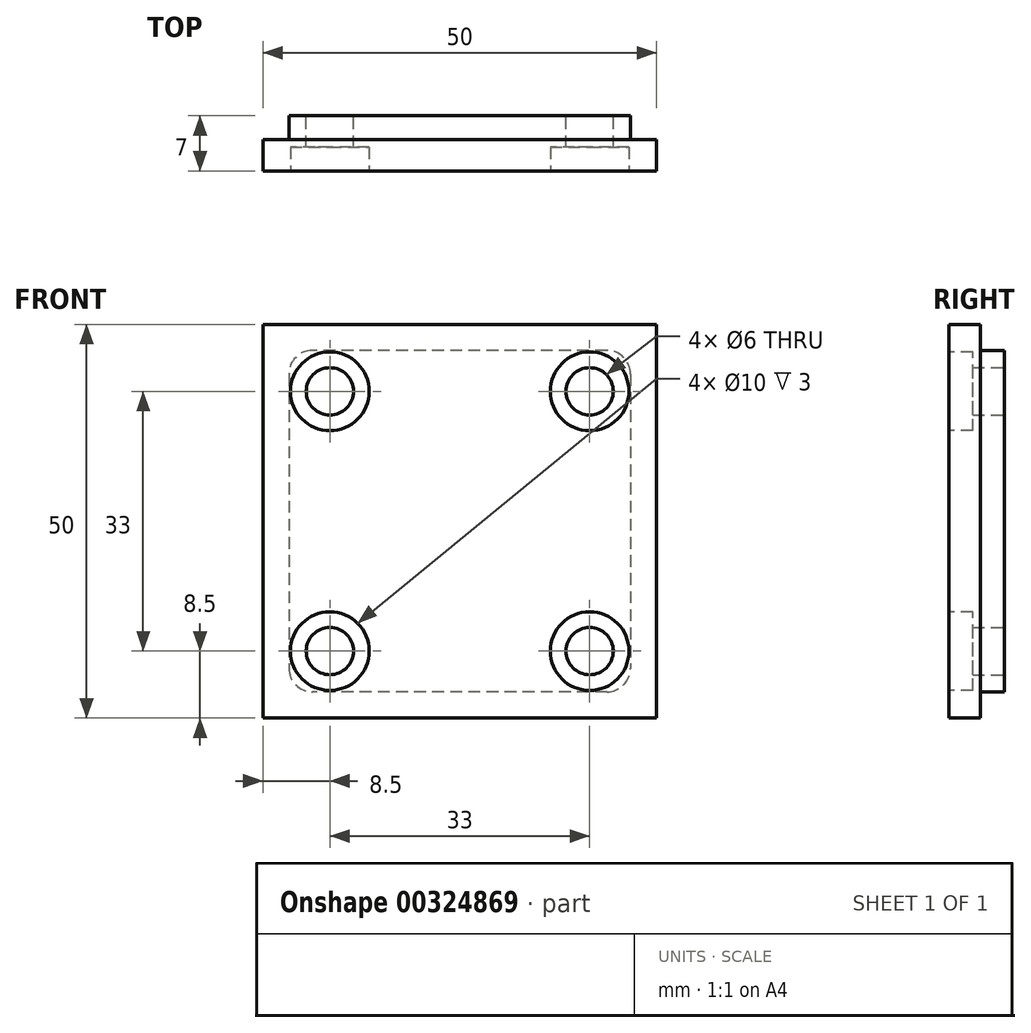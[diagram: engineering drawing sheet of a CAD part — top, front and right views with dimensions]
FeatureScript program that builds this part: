
annotation { "Feature Type Name" : "Feature", "Feature Type Description" : "" }
export const myFeature = defineFeature(function(context is Context, id is Id, definition is map)
    precondition{}
    {
        {
            var Q0;
            Q0=qCreatedBy(makeId("Front.planeOp"),FACE);
            var sketch = newSketch(context, id + "F0", { "sketchPlane" : qUnion([Q0])});
            skLineSegment(sketch, "E0.bottom", {"start": v(-25, 25) * mm, "end": v(25, 25) * mm});
            skLineSegment(sketch, "E0.top", {"start": v(-25, -25) * mm, "end": v(25, -25) * mm});
            skLineSegment(sketch, "E0.left", {"start": v(-25, 25) * mm, "end": v(-25, -25) * mm});
            skLineSegment(sketch, "E0.right", {"start": v(25, 25) * mm, "end": v(25, -25) * mm});
            skPoint(sketch, "E0.middle", {"position": v(0, 0) * mm});
            skSolve(sketch);
        }
        {
            var Q0;
            Q0=makeQuery(id+"F0.imprint","IMPRINT",FACE,{"disambiguationData":[TD([[makeQuery(id+"F0.imprint","IMPRINT",EDGE,{"derivedFrom":sQuery(id+"F0.wireOp",EDGE,"E0.bottom")}),-1.0]])]});
            extrude(context, id + "F1", {"entities" : qUnion([Q0]), "oppositeDirection" : true, "depth" : 4 * mm});
        }
        {
            var Q0;
            Q0=makeQuery(id+"F1.opExtrude","CAP_FACE",FACE,{"disambiguationData":[OSD([sQuery(id+"F0.wireOp",EDGE,"E0.bottom"),sQuery(id+"F0.wireOp",EDGE,"E0.top"),sQuery(id+"F0.wireOp",EDGE,"E0.left"),sQuery(id+"F0.wireOp",EDGE,"E0.right")])],"isStart":false});
            var sketch = newSketch(context, id + "F2", { "sketchPlane" : qUnion([Q0])});
            skLineSegment(sketch, "E1.bottom", {"start": v(-21.7, 21.7) * mm, "end": v(21.7, 21.7) * mm});
            skLineSegment(sketch, "E1.top", {"start": v(-21.7, -21.7) * mm, "end": v(21.7, -21.7) * mm});
            skLineSegment(sketch, "E1.left", {"start": v(-21.7, 21.7) * mm, "end": v(-21.7, -21.7) * mm});
            skLineSegment(sketch, "E1.right", {"start": v(21.7, 21.7) * mm, "end": v(21.7, -21.7) * mm});
            skPoint(sketch, "E1.middle", {"position": v(0, 0) * mm});
            skSolve(sketch);
        }
        {
            var Q0;
            Q0=makeQuery(id+"F2.imprint","IMPRINT",FACE,{"disambiguationData":[TD([[makeQuery(id+"F2.imprint","IMPRINT",EDGE,{"derivedFrom":sQuery(id+"F2.wireOp",EDGE,"E1.bottom")}),-1.0]])]});
            extrude(context, id + "F3", {"entities" : qUnion([Q0]), "operationType" : NewBodyOperationType.ADD, "depth" : 3 * mm});
        }
        {
            var Q0;
            Q0=makeQuery(id+"F3.opExtrude","CAP_FACE",FACE,{"disambiguationData":[OSD([sQuery(id+"F2.wireOp",EDGE,"E1.bottom"),sQuery(id+"F2.wireOp",EDGE,"E1.top"),sQuery(id+"F2.wireOp",EDGE,"E1.left"),sQuery(id+"F2.wireOp",EDGE,"E1.right")])],"isStart":false});
            var sketch = newSketch(context, id + "F4", { "sketchPlane" : qUnion([Q0])});
            skLineSegment(sketch, "E2", {"start": v(-21.7, 21.7) * mm, "end": v(21.7, -21.7) * mm, "construction": true});
            skLineSegment(sketch, "E3", {"start": v(21.7, 21.7) * mm, "end": v(-21.7, -21.7) * mm, "construction": true});
            skLineSegment(sketch, "E4.bottom", {"start": v(-16.5, 16.5) * mm, "end": v(16.5, 16.5) * mm, "construction": true});
            skLineSegment(sketch, "E4.top", {"start": v(-16.5, -16.5) * mm, "end": v(16.5, -16.5) * mm, "construction": true});
            skLineSegment(sketch, "E4.left", {"start": v(-16.5, 16.5) * mm, "end": v(-16.5, -16.5) * mm, "construction": true});
            skLineSegment(sketch, "E4.right", {"start": v(16.5, 16.5) * mm, "end": v(16.5, -16.5) * mm, "construction": true});
            skPoint(sketch, "E4.middle", {"position": v(0, 0) * mm});
            skCircle(sketch, "E5", {"center": v(-16.5, 16.5) * mm, "radius": 3 * mm});
            skCircle(sketch, "E6", {"center": v(16.5, 16.5) * mm, "radius": 3 * mm});
            skCircle(sketch, "E7", {"center": v(-16.5, -16.5) * mm, "radius": 3 * mm});
            skCircle(sketch, "E8", {"center": v(16.5, -16.5) * mm, "radius": 3 * mm});
            skSolve(sketch);
        }
        {
            var Q0;
            Q0=makeQuery(id+"F4.imprint","IMPRINT",FACE,{"disambiguationData":[TD([[makeQuery(id+"F4.imprint","IMPRINT",EDGE,{"derivedFrom":sQuery(id+"F4.wireOp",EDGE,"E5")}),1.0]])]});
            var Q1;
            Q1=makeQuery(id+"F4.imprint","IMPRINT",FACE,{"disambiguationData":[TD([[makeQuery(id+"F4.imprint","IMPRINT",EDGE,{"derivedFrom":sQuery(id+"F4.wireOp",EDGE,"E6")}),1.0]])]});
            var Q2;
            Q2=makeQuery(id+"F4.imprint","IMPRINT",FACE,{"disambiguationData":[TD([[makeQuery(id+"F4.imprint","IMPRINT",EDGE,{"derivedFrom":sQuery(id+"F4.wireOp",EDGE,"E8")}),1.0]])]});
            var Q3;
            Q3=makeQuery(id+"F4.imprint","IMPRINT",FACE,{"disambiguationData":[TD([[makeQuery(id+"F4.imprint","IMPRINT",EDGE,{"derivedFrom":sQuery(id+"F4.wireOp",EDGE,"E7")}),1.0]])]});
            var Q4;
            Q4=makeQuery(id+"F4.imprint","IMPRINT",FACE,{"disambiguationData":[TD([[makeQuery(id+"F4.imprint","IMPRINT",EDGE,{"derivedFrom":sQuery(id+"F4.wireOp",EDGE,"QwKJkzou-eQ0R-DmLM-VaWs-TZL8aThNHikG")}),1.0]])]});
            extrude(context, id + "F5", {"entities" : qUnion([Q0, Q1, Q2, Q3, Q4]), "operationType" : NewBodyOperationType.REMOVE, "oppositeDirection" : true, "depth" : 25 * mm});
        }
        {
            var Q0;
            Q0=makeQuery(id+"F1.opExtrude","CAP_FACE",FACE,{"disambiguationData":[OSD([sQuery(id+"F0.wireOp",EDGE,"E0.bottom"),sQuery(id+"F0.wireOp",EDGE,"E0.top"),sQuery(id+"F0.wireOp",EDGE,"E0.left"),sQuery(id+"F0.wireOp",EDGE,"E0.right")])],"isStart":true});
            var sketch = newSketch(context, id + "F6", { "sketchPlane" : qUnion([Q0])});
            skCircle(sketch, "E9", {"center": v(-16.5, 16.5) * mm, "radius": 5 * mm});
            skCircle(sketch, "E10.1.0", {"center": v(-16.5, -16.5) * mm, "radius": 5 * mm});
            skCircle(sketch, "E10.2.0", {"center": v(16.5, -16.5) * mm, "radius": 5 * mm});
            skCircle(sketch, "E10.3.0", {"center": v(16.5, 16.5) * mm, "radius": 5 * mm});
            skPoint(sketch, "E10.center", {"position": v(0, 0) * mm});
            skSolve(sketch);
        }
        {
            var Q0;
            Q0=makeQuery(id+"F6.imprint","IMPRINT",FACE,{"disambiguationData":[TD([[makeQuery(id+"F6.imprint","IMPRINT",EDGE,{"derivedFrom":sQuery(id+"F6.wireOp",EDGE,"E9")}),1.0]])]});
            var Q1;
            Q1=makeQuery(id+"F6.imprint","IMPRINT",FACE,{"disambiguationData":[TD([[makeQuery(id+"F6.imprint","IMPRINT",EDGE,{"derivedFrom":sQuery(id+"F6.wireOp",EDGE,"E10.3.0")}),1.0]])]});
            var Q2;
            Q2=makeQuery(id+"F6.imprint","IMPRINT",FACE,{"disambiguationData":[TD([[makeQuery(id+"F6.imprint","IMPRINT",EDGE,{"derivedFrom":sQuery(id+"F6.wireOp",EDGE,"E10.2.0")}),1.0]])]});
            var Q3;
            Q3=makeQuery(id+"F6.imprint","IMPRINT",FACE,{"disambiguationData":[TD([[makeQuery(id+"F6.imprint","IMPRINT",EDGE,{"derivedFrom":sQuery(id+"F6.wireOp",EDGE,"E10.1.0")}),1.0]])]});
            extrude(context, id + "F7", {"entities" : qUnion([Q0, Q1, Q2, Q3]), "operationType" : NewBodyOperationType.REMOVE, "oppositeDirection" : true, "depth" : 3 * mm});
        }
        {
            var Q0;
            Q0=makeQuery(id+"F3.opExtrude","SWEPT_EDGE",EDGE,{"disambiguationData":[OSD([sQuery(id+"F2.wireOp",EDGE,"E1.bottom"),sQuery(id+"F2.wireOp",EDGE,"E1.left")])]});
            var Q1;
            Q1=makeQuery(id+"F3.opExtrude","SWEPT_EDGE",EDGE,{"disambiguationData":[OSD([sQuery(id+"F2.wireOp",EDGE,"E1.bottom"),sQuery(id+"F2.wireOp",EDGE,"E1.right")])]});
            var Q2;
            Q2=makeQuery(id+"F3.opExtrude","SWEPT_EDGE",EDGE,{"disambiguationData":[OSD([sQuery(id+"F2.wireOp",EDGE,"E1.top"),sQuery(id+"F2.wireOp",EDGE,"E1.right")])]});
            var Q3;
            Q3=makeQuery(id+"F3.opExtrude","SWEPT_EDGE",EDGE,{"disambiguationData":[OSD([sQuery(id+"F2.wireOp",EDGE,"E1.top"),sQuery(id+"F2.wireOp",EDGE,"E1.left")])]});
            fillet(context, id + "F8", {"entities" : qUnion([Q0, Q1, Q2, Q3]), "radius" : 3 * mm, "tangentPropagation" : true, "allowEdgeOverflow" : false});
        }
    });
